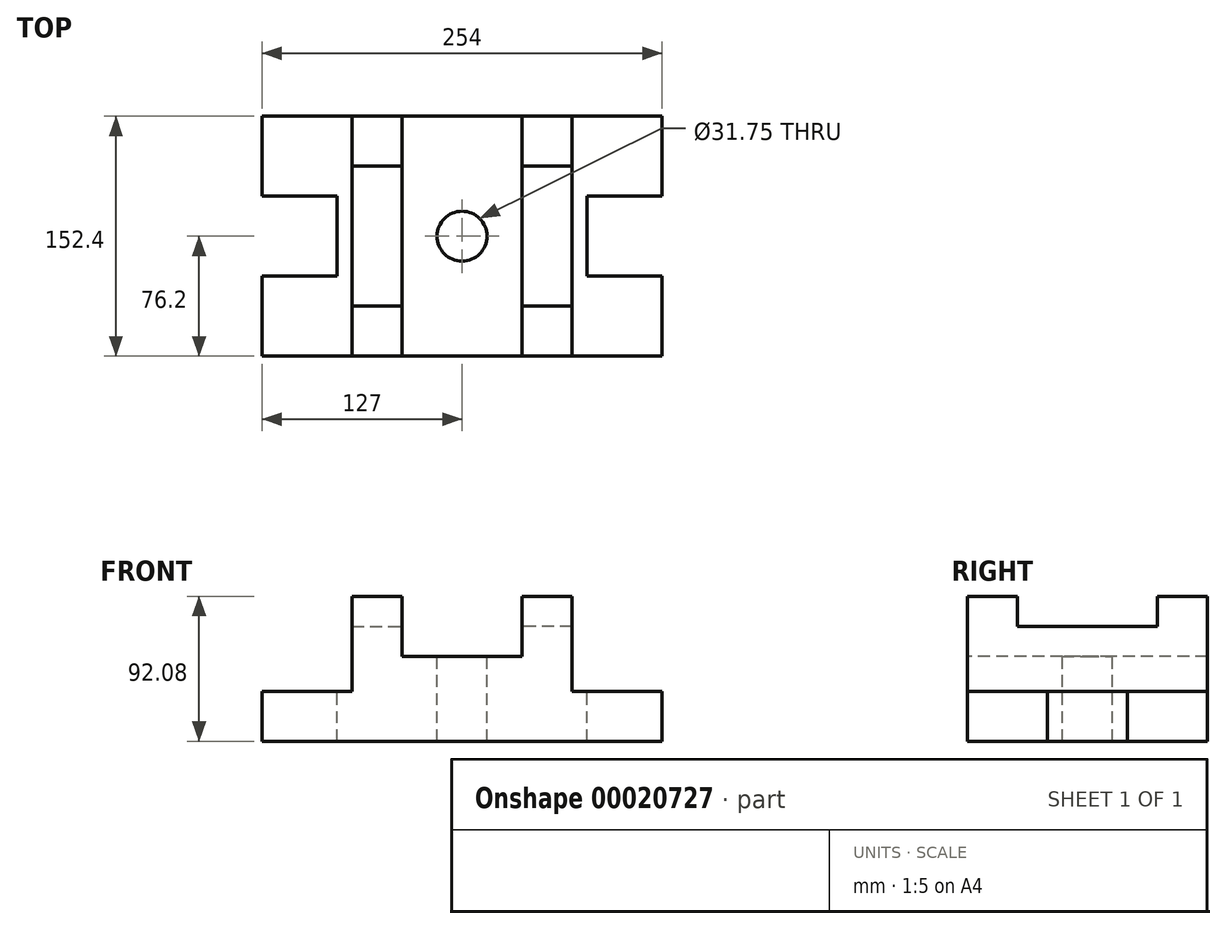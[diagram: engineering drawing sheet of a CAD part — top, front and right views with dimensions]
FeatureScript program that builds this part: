
annotation { "Feature Type Name" : "Feature", "Feature Type Description" : "" }
export const myFeature = defineFeature(function(context is Context, id is Id, definition is map)
    precondition{}
    {
        {
            var Q0;
            Q0=qCreatedBy(makeId("Front.planeOp"),FACE);
            var sketch = newSketch(context, id + "F0", { "sketchPlane" : qUnion([Q0])});
            skLineSegment(sketch, "E0", {"start": v(0, 0) * mm, "end": v(0, 53.98) * mm});
            skLineSegment(sketch, "E1", {"start": v(0, 53.98) * mm, "end": v(38.1, 53.98) * mm});
            skLineSegment(sketch, "E2", {"start": v(38.1, 53.98) * mm, "end": v(38.1, 92.08) * mm});
            skLineSegment(sketch, "E3", {"start": v(38.1, 92.08) * mm, "end": v(69.85, 92.08) * mm});
            skLineSegment(sketch, "E4", {"start": v(69.85, 92.08) * mm, "end": v(69.85, 31.75) * mm});
            skLineSegment(sketch, "E5", {"start": v(69.85, 31.75) * mm, "end": v(127, 31.75) * mm});
            skLineSegment(sketch, "E6", {"start": v(127, 31.75) * mm, "end": v(127, 0) * mm});
            skLineSegment(sketch, "E7", {"start": v(127, 0) * mm, "end": v(0, 0) * mm});
            skSolve(sketch);
        }
        {
            var Q0;
            Q0 = qSketchRegion(id + "F0", true);
            extrude(context, id + "F1", {"entities" : qUnion([Q0]), "oppositeDirection" : true, "depth" : 76.2 * mm});
        }
        {
            var Q0;
            Q0=makeQuery(id+"F1.opExtrude","SWEPT_FACE",FACE,{"disambiguationData":[OSD([sQuery(id+"F0.wireOp",EDGE,"E3")])]});
            var sketch = newSketch(context, id + "F2", { "sketchPlane" : qUnion([Q0])});
            skLineSegment(sketch, "E8", {"start": v(69.85, 76.2) * mm, "end": v(69.85, 31.75) * mm});
            skLineSegment(sketch, "E9", {"start": v(69.85, 31.75) * mm, "end": v(38.1, 31.75) * mm});
            skLineSegment(sketch, "E10", {"start": v(38.1, 31.75) * mm, "end": v(38.1, 76.2) * mm});
            skLineSegment(sketch, "E11", {"start": v(38.1, 76.2) * mm, "end": v(69.85, 76.2) * mm});
            skSolve(sketch);
        }
        {
            var Q0;
            Q0=makeQuery(id+"F2.imprint","IMPRINT",FACE,{"disambiguationData":[TD([[makeQuery(id+"F2.imprint","IMPRINT",EDGE,{"derivedFrom":sQuery(id+"F2.wireOp",EDGE,"E8")}),-1.0]])]});
            extrude(context, id + "F3", {"entities" : qUnion([Q0]), "operationType" : NewBodyOperationType.REMOVE, "oppositeDirection" : true, "depth" : 19.05 * mm});
        }
        {
            var Q0;
            Q0=makeQuery(id+"F1.opExtrude","SWEPT_FACE",FACE,{"disambiguationData":[OSD([sQuery(id+"F0.wireOp",EDGE,"E5")])]});
            var sketch = newSketch(context, id + "F4", { "sketchPlane" : qUnion([Q0])});
            skLineSegment(sketch, "E12.bottom", {"start": v(127, 76.2) * mm, "end": v(79.38, 76.2) * mm});
            skLineSegment(sketch, "E12.top", {"start": v(127, 50.8) * mm, "end": v(79.38, 50.8) * mm});
            skLineSegment(sketch, "E12.left", {"start": v(127, 76.2) * mm, "end": v(127, 50.8) * mm});
            skLineSegment(sketch, "E12.right", {"start": v(79.38, 76.2) * mm, "end": v(79.38, 50.8) * mm});
            skSolve(sketch);
        }
        {
            var Q0;
            Q0 = qSketchRegion(id + "F4", true);
            extrude(context, id + "F5", {"entities" : qUnion([Q0]), "operationType" : NewBodyOperationType.REMOVE, "endBound" : BoundingType.UP_TO_NEXT, "oppositeDirection" : true, "depth" : 25.4 * mm});
        }
        {
            var Q0;
            Q0=makeQuery(id+"F1.opExtrude","SWEPT_FACE",FACE,{"disambiguationData":[OSD([sQuery(id+"F0.wireOp",EDGE,"E1")])]});
            var sketch = newSketch(context, id + "F6", { "sketchPlane" : qUnion([Q0])});
            skArc(sketch, "E13", {"start": v(0, 60.33) * mm, "mid": v(11.23, 64.97) * mm, "end": v(15.87, 76.2) * mm});
            skLineSegment(sketch, "E14", {"start": v(15.87, 76.2) * mm, "end": v(0, 76.2) * mm});
            skLineSegment(sketch, "E15", {"start": v(0, 60.33) * mm, "end": v(0, 76.2) * mm});
            skSolve(sketch);
        }
        {
            var Q0;
            Q0 = qSketchRegion(id + "F6", true);
            extrude(context, id + "F7", {"entities" : qUnion([Q0]), "operationType" : NewBodyOperationType.REMOVE, "endBound" : BoundingType.UP_TO_NEXT, "oppositeDirection" : true, "depth" : 25.4 * mm});
        }
        {
            var Q0;
            Q0=makeQuery(id+"F1.opExtrude","SWEPT_BODY",BODY,{"disambiguationData":[OSD([sQuery(id+"F0.wireOp",EDGE,"E0"),sQuery(id+"F0.wireOp",EDGE,"E1"),sQuery(id+"F0.wireOp",EDGE,"E2"),sQuery(id+"F0.wireOp",EDGE,"E3"),sQuery(id+"F0.wireOp",EDGE,"E4"),sQuery(id+"F0.wireOp",EDGE,"E5"),sQuery(id+"F0.wireOp",EDGE,"E6"),sQuery(id+"F0.wireOp",EDGE,"E7")])]});
            var Q1;
            Q1=makeQuery(id+"F1.opExtrude","CAP_FACE",FACE,{"disambiguationData":[OSD([sQuery(id+"F0.wireOp",EDGE,"E0"),sQuery(id+"F0.wireOp",EDGE,"E1"),sQuery(id+"F0.wireOp",EDGE,"E2"),sQuery(id+"F0.wireOp",EDGE,"E3"),sQuery(id+"F0.wireOp",EDGE,"E4"),sQuery(id+"F0.wireOp",EDGE,"E5"),sQuery(id+"F0.wireOp",EDGE,"E6"),sQuery(id+"F0.wireOp",EDGE,"E7")])],"isStart":false});
            mirror(context, id + "F8", {"operationType" : NewBodyOperationType.ADD, "entities" : qUnion([Q0]), "mirrorPlane" : qUnion([Q1])});
        }
        {
            var Q0;
            Q0=makeQuery(id+"F1.opExtrude","SWEPT_BODY",BODY,{"disambiguationData":[OSD([sQuery(id+"F0.wireOp",EDGE,"E0"),sQuery(id+"F0.wireOp",EDGE,"E1"),sQuery(id+"F0.wireOp",EDGE,"E2"),sQuery(id+"F0.wireOp",EDGE,"E3"),sQuery(id+"F0.wireOp",EDGE,"E4"),sQuery(id+"F0.wireOp",EDGE,"E5"),sQuery(id+"F0.wireOp",EDGE,"E6"),sQuery(id+"F0.wireOp",EDGE,"E7")])]});
            var Q1;
            Q1=makeQuery(id+"F1.opExtrude","SWEPT_FACE",FACE,{"disambiguationData":[OSD([sQuery(id+"F0.wireOp",EDGE,"E0")])]});
            mirror(context, id + "F9", {"operationType" : NewBodyOperationType.ADD, "entities" : qUnion([Q0]), "mirrorPlane" : qUnion([Q1])});
        }
    });
